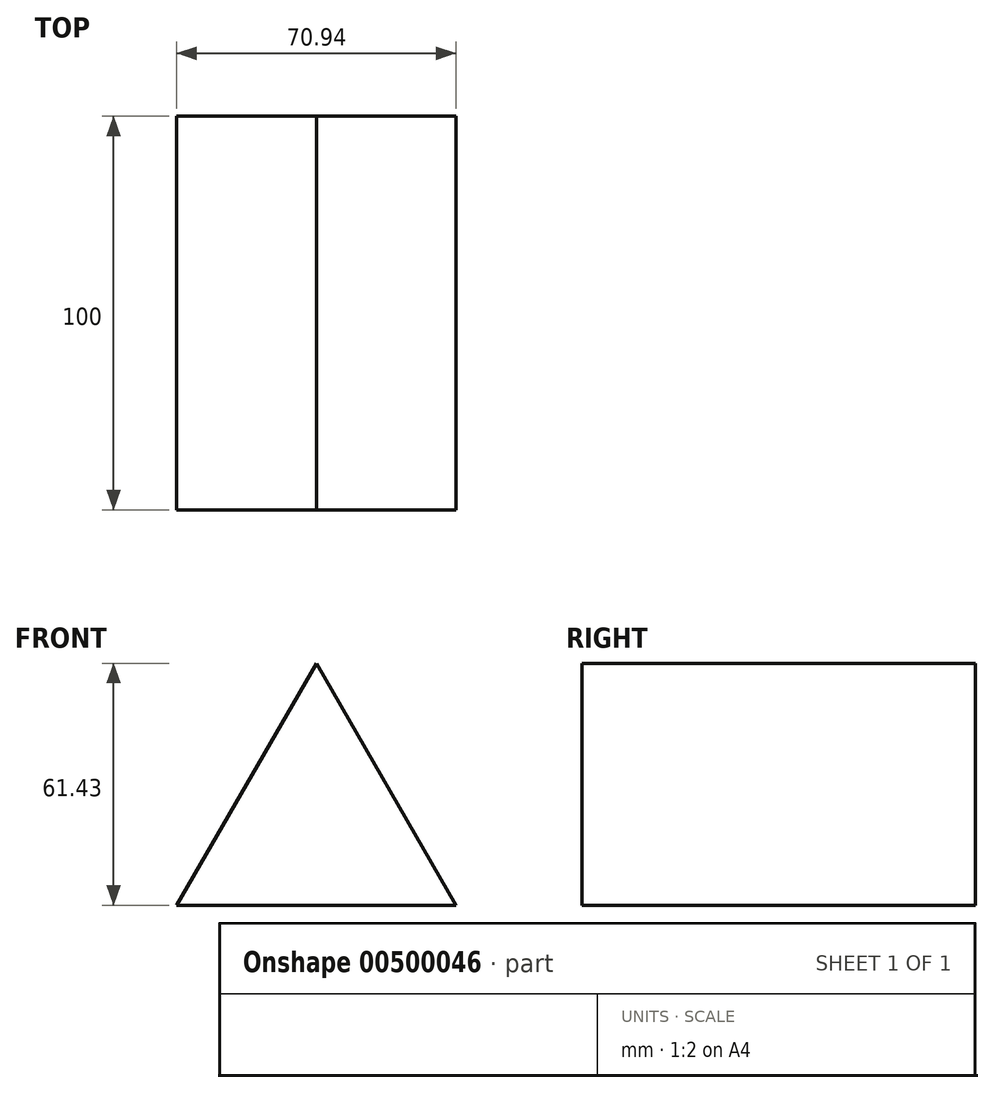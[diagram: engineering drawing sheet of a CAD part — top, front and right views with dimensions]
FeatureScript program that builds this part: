
annotation { "Feature Type Name" : "Feature", "Feature Type Description" : "" }
export const myFeature = defineFeature(function(context is Context, id is Id, definition is map)
    precondition{}
    {
        {
            var Q0;
            Q0=qCreatedBy(makeId("Front.planeOp"),FACE);
            var sketch = newSketch(context, id + "F0", { "sketchPlane" : qUnion([Q0])});
            skCircle(sketch, "E0.cCircle", {"center": v(0, 0) * mm, "radius": 40.95 * mm, "construction": true});
            skLineSegment(sketch, "E0.0", {"start": v(35.47, -20.48) * mm, "end": v(-35.47, -20.48) * mm});
            skLineSegment(sketch, "E0.1", {"start": v(-35.47, -20.48) * mm, "end": v(0, 40.95) * mm});
            skLineSegment(sketch, "E0.2", {"start": v(0, 40.95) * mm, "end": v(35.47, -20.48) * mm});
            skSolve(sketch);
        }
        {
            var Q0;
            Q0 = qSketchRegion(id + "F0", true);
            extrude(context, id + "F1", {"entities" : qUnion([Q0]), "endBound" : BoundingType.SYMMETRIC, "depth" : 100 * mm});
        }
    });
